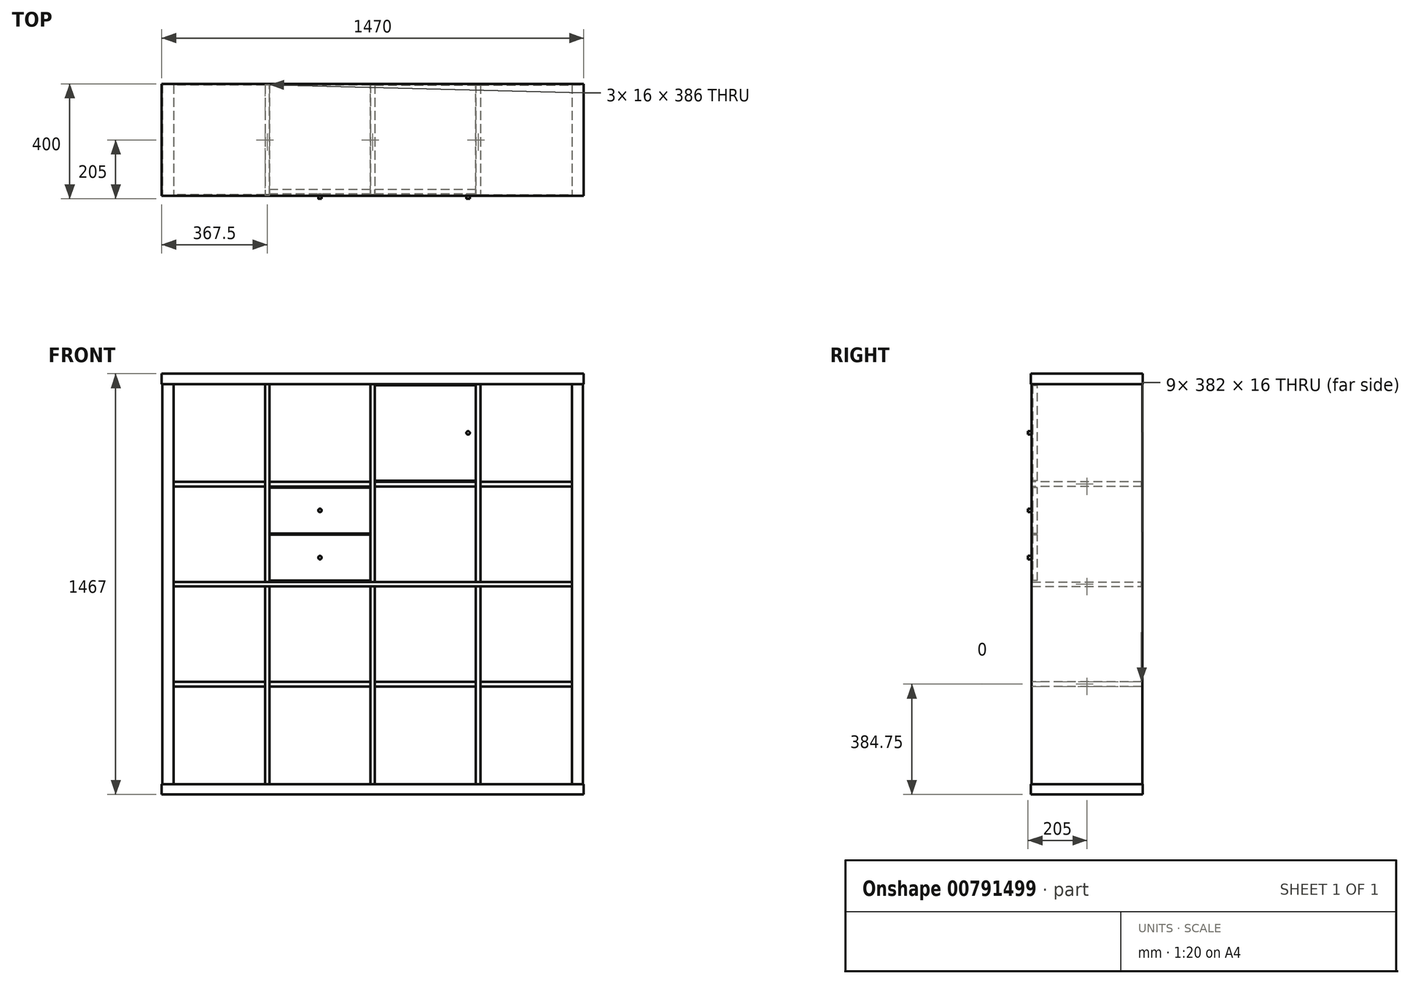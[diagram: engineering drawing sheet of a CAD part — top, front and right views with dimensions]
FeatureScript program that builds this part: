
annotation { "Feature Type Name" : "Feature", "Feature Type Description" : "" }
export const myFeature = defineFeature(function(context is Context, id is Id, definition is map)
    precondition{}
    {
        {
            var Q0;
            Q0=qCreatedBy(makeId("Top.planeOp"),FACE);
            var sketch = newSketch(context, id + "F0", { "sketchPlane" : qUnion([Q0])});
            skLineSegment(sketch, "E0.bottom", {"start": v(367.5, -97.5) * mm, "end": v(-367.5, -97.5) * mm});
            skLineSegment(sketch, "E0.top", {"start": v(367.5, 97.5) * mm, "end": v(-367.5, 97.5) * mm});
            skLineSegment(sketch, "E0.left", {"start": v(367.5, -97.5) * mm, "end": v(367.5, 97.5) * mm});
            skLineSegment(sketch, "E0.right", {"start": v(-367.5, -97.5) * mm, "end": v(-367.5, 97.5) * mm});
            skPoint(sketch, "E0.middle", {"position": v(0, 0) * mm});
            skLineSegment(sketch, "E1", {"start": v(-365.5, 97.5) * mm, "end": v(-365.5, -97.5) * mm});
            skLineSegment(sketch, "E2", {"start": v(-329.5, 97.5) * mm, "end": v(-329.5, -97.5) * mm});
            skSolve(sketch);
        }
        {
            var Q0;
            Q0 = qSketchRegion(id + "F0", true);
            var Q1;
            Q1=makeQuery(id+"F0.imprint","IMPRINT",FACE,{"disambiguationData":[TD([[makeQuery(id+"F0.imprint","IMPRINT",EDGE,{"derivedFrom":sQuery(id+"F0.wireOp",EDGE,"E0.bottom")}),-1.0]])]});
            extrude(context, id + "F1", {"entities" : qUnion([Q0, Q1]), "depth" : 36 * mm, "offsetDistance" : 25 * mm});
        }
        {
            var Q0;
            Q0=makeQuery(id+"F1.opExtrude","CAP_FACE",FACE,{"disambiguationData":[OSD([sQuery(id+"F0.wireOp",EDGE,"E0.bottom"),sQuery(id+"F0.wireOp",EDGE,"E0.top"),sQuery(id+"F0.wireOp",EDGE,"E0.left"),sQuery(id+"F0.wireOp",EDGE,"E0.right")])],"isStart":false});
            var sketch = newSketch(context, id + "F2", { "sketchPlane" : qUnion([Q0])});
            skLineSegment(sketch, "E3", {"start": v(-365.5, 97.5) * mm, "end": v(-365.5, -97.5) * mm});
            skLineSegment(sketch, "E4", {"start": v(-326.5, 97.5) * mm, "end": v(-326.5, -97.5) * mm});
            skLineSegment(sketch, "E5", {"start": v(-326.5, -95.5) * mm, "end": v(-365.5, -95.5) * mm});
            skSolve(sketch);
        }
        {
            var Q0;
            {var subQ3=sQuery(id+"F2.wireOp",EDGE,"E5");Q0=makeQuery(id+"F2.imprint","IMPRINT",FACE,{"disambiguationData":[TD([[makeQuery(id+"F2.imprint","IMPRINT",EDGE,{"derivedFrom":subQ3}),-1.0]])]});}
            extrude(context, id + "F3", {"entities" : qUnion([Q0]), "operationType" : NewBodyOperationType.ADD, "depth" : (1395 / 2) * mm, "offsetDistance" : 25 * mm});
        }
        {
            var Q0;
            Q0=makeQuery(id+"F3.opExtrude","SWEPT_FACE",FACE,{"disambiguationData":[OSD([sQuery(id+"F2.wireOp",EDGE,"E4")])]});
            var sketch = newSketch(context, id + "F4", { "sketchPlane" : qUnion([Q0])});
            skLineSegment(sketch, "E6.0", {"start": v(97.5, 733.5) * mm, "end": v(-95.5, 733.5) * mm});
            skLineSegment(sketch, "E7", {"start": v(97.5, 725.5) * mm, "end": v(-95.5, 725.5) * mm});
            skLineSegment(sketch, "E8", {"start": v(-93.5, 725.5) * mm, "end": v(-93.5, 733.5) * mm});
            skLineSegment(sketch, "E9", {"start": v(97.5, 384.75) * mm, "end": v(-95.5, 384.75) * mm, "construction": true});
            skLineSegment(sketch, "E10", {"start": v(97.5, 392.75) * mm, "end": v(-95.5, 392.75) * mm});
            skLineSegment(sketch, "E11", {"start": v(97.5, 376.75) * mm, "end": v(-95.5, 376.75) * mm});
            skLineSegment(sketch, "E12", {"start": v(-93.5, 392.75) * mm, "end": v(-93.5, 376.75) * mm});
            skSolve(sketch);
        }
        {
            var Q0;
            Q0 = qSketchRegion(id + "F4", true);
            var Q1;
            {var subQ3=sQuery(id+"F4.wireOp",EDGE,"E8");Q1=makeQuery(id+"F4.imprint","IMPRINT",FACE,{"disambiguationData":[TD([[makeQuery(id+"F4.imprint","IMPRINT",EDGE,{"derivedFrom":subQ3}),-1.0]])]});}
            var Q2;
            {var subQ3=sQuery(id+"F4.wireOp",EDGE,"E12");Q2=makeQuery(id+"F4.imprint","IMPRINT",FACE,{"disambiguationData":[TD([[makeQuery(id+"F4.imprint","IMPRINT",EDGE,{"derivedFrom":subQ3}),1.0]])]});}
            var Q3;
            Q3=makeQuery(id+"F1.opExtrude","SWEPT_FACE",FACE,{"disambiguationData":[OSD([sQuery(id+"F0.wireOp",EDGE,"E0.left")])]});
            extrude(context, id + "F5", {"entities" : qUnion([Q0, Q1, Q2]), "operationType" : NewBodyOperationType.ADD, "endBound" : BoundingType.UP_TO_SURFACE, "depth" : 25 * mm, "endBoundEntityFace" : qUnion([Q3]), "offsetDistance" : 25 * mm});
        }
        {
            var Q0;
            Q0=makeQuery(id+"F1.opExtrude","CAP_FACE",FACE,{"disambiguationData":[OSD([sQuery(id+"F0.wireOp",EDGE,"E0.bottom"),sQuery(id+"F0.wireOp",EDGE,"E0.top"),sQuery(id+"F0.wireOp",EDGE,"E0.left"),sQuery(id+"F0.wireOp",EDGE,"E0.right")])],"isStart":false});
            var sketch = newSketch(context, id + "F6", { "sketchPlane" : qUnion([Q0])});
            skLineSegment(sketch, "E13", {"start": v(-326.5, 1) * mm, "end": v(367.5, 1) * mm, "construction": true});
            skLineSegment(sketch, "E14", {"start": v(0, 0) * mm, "end": v(0, 97.5) * mm, "construction": true});
            skLineSegment(sketch, "E15", {"start": v(0, 0) * mm, "end": v(0, -97.5) * mm, "construction": true});
            skLineSegment(sketch, "E16", {"start": v(8, 97.5) * mm, "end": v(8, -97.5) * mm});
            skLineSegment(sketch, "E17", {"start": v(-8, 97.5) * mm, "end": v(-8, -97.5) * mm});
            skLineSegment(sketch, "E18", {"start": v(8, -95.5) * mm, "end": v(-8, -95.5) * mm});
            skLineSegment(sketch, "E19.0", {"start": v(367.5, -97.5) * mm, "end": v(367.5, 97.5) * mm});
            skLineSegment(sketch, "E20", {"start": v(359.5, 97.5) * mm, "end": v(359.5, -97.5) * mm});
            skLineSegment(sketch, "E21", {"start": v(367.5, -95.5) * mm, "end": v(359.5, -95.5) * mm});
            skSolve(sketch);
        }
        {
            var Q0;
            Q0 = qSketchRegion(id + "F6", true);
            var Q1;
            {var subQ5=sQuery(id+"F6.wireOp",EDGE,"E18");Q1=makeQuery(id+"F6.imprint","IMPRINT",FACE,{"disambiguationData":[TD([[makeQuery(id+"F6.imprint","IMPRINT",EDGE,{"derivedFrom":subQ5}),-1.0]])]});}
            var Q2;
            {var subQ5=sQuery(id+"F6.wireOp",EDGE,"E21");Q2=makeQuery(id+"F6.imprint","IMPRINT",FACE,{"disambiguationData":[TD([[makeQuery(id+"F6.imprint","IMPRINT",EDGE,{"derivedFrom":subQ5}),-1.0]])]});}
            var Q3;
            Q3=makeQuery(id+"F5.opExtrude","SWEPT_FACE",FACE,{"disambiguationData":[OSD([sQuery(id+"F4.wireOp",EDGE,"E7")])]});
            extrude(context, id + "F7", {"entities" : qUnion([Q0, Q1, Q2]), "operationType" : NewBodyOperationType.ADD, "endBound" : BoundingType.UP_TO_SURFACE, "depth" : 25 * mm, "endBoundEntityFace" : qUnion([Q3]), "offsetDistance" : 25 * mm});
        }
        {
            var Q0;
            Q0=makeQuery(id+"F1.opExtrude","SWEPT_BODY",BODY,{"disambiguationData":[OSD([sQuery(id+"F0.wireOp",EDGE,"E0.bottom"),sQuery(id+"F0.wireOp",EDGE,"E0.top"),sQuery(id+"F0.wireOp",EDGE,"E0.left"),sQuery(id+"F0.wireOp",EDGE,"E0.right")])]});
            var Q1;
            Q1=makeQuery(id+"F5.boolean.opBoolean","MERGE",FACE,{"derivedFrom":[makeQuery(id+"F3.opExtrude","CAP_FACE",FACE,{"disambiguationData":[OSD([sQuery(id+"F0.wireOp",EDGE,"E0.top"),sQuery(id+"F2.wireOp",EDGE,"E3"),sQuery(id+"F2.wireOp",EDGE,"E4"),sQuery(id+"F2.wireOp",EDGE,"E5")])],"isStart":false}),makeQuery(id+"F5.opExtrude","SWEPT_FACE",FACE,{"disambiguationData":[OSD([sQuery(id+"F4.wireOp",EDGE,"E6.0")])]})]});
            mirror(context, id + "F8", {"operationType" : NewBodyOperationType.ADD, "entities" : qUnion([Q0]), "mirrorPlane" : qUnion([Q1])});
        }
        {
            var Q0;
            Q0=makeQuery(id+"F1.opExtrude","SWEPT_BODY",BODY,{"disambiguationData":[OSD([sQuery(id+"F0.wireOp",EDGE,"E0.bottom"),sQuery(id+"F0.wireOp",EDGE,"E0.top"),sQuery(id+"F0.wireOp",EDGE,"E0.left"),sQuery(id+"F0.wireOp",EDGE,"E0.right")])]});
            var Q1;
            {var subQ0=sQuery(id+"F0.wireOp",EDGE,"E0.left");var subQ1=makeQuery(id+"F7.boolean.opBoolean","MERGE",FACE,{"derivedFrom":[makeQuery(id+"F1.opExtrude","SWEPT_FACE",FACE,{"disambiguationData":[OSD([subQ0])]}),makeQuery(id+"F5.opExtrude","CAP_FACE",FACE,{"disambiguationData":[OSD([subQ0]),OD(0.0)],"isStart":false}),makeQuery(id+"F5.opExtrude","CAP_FACE",FACE,{"disambiguationData":[OSD([subQ0]),OD(1.0)],"isStart":false}),makeQuery(id+"F7.opExtrude","SWEPT_FACE",FACE,{"disambiguationData":[OSD([sQuery(id+"F6.wireOp",EDGE,"E19.0")])]})]});Q1=makeQuery(id+"F8.boolean.opBoolean","MERGE",FACE,{"derivedFrom":[subQ1,makeQuery(id+"F8.opPattern","COPY",FACE,{"derivedFrom":subQ1,"instanceName":"1"})]});}
            mirror(context, id + "F9", {"operationType" : NewBodyOperationType.ADD, "entities" : qUnion([Q0]), "mirrorPlane" : qUnion([Q1])});
        }
        {
            var Q0;
            Q0=makeQuery(id+"F1.opExtrude","SWEPT_BODY",BODY,{"disambiguationData":[OSD([sQuery(id+"F0.wireOp",EDGE,"E0.bottom"),sQuery(id+"F0.wireOp",EDGE,"E0.top"),sQuery(id+"F0.wireOp",EDGE,"E0.left"),sQuery(id+"F0.wireOp",EDGE,"E0.right")])]});
            var Q1;
            {var subQ0=sQuery(id+"F2.wireOp",EDGE,"E4");var subQ1=sQuery(id+"F0.wireOp",EDGE,"E0.left");var subQ2=sQuery(id+"F0.wireOp",EDGE,"E0.top");var subQ3=makeQuery(id+"F1.opExtrude","SWEPT_FACE",FACE,{"disambiguationData":[OSD([subQ2])]});var subQ4=makeQuery(id+"F3.opExtrude","SWEPT_FACE",FACE,{"disambiguationData":[OSD([subQ2])]});var subQ5=makeQuery(id+"F3.boolean.opBoolean","SPLIT",EDGE,{"disambiguationData":[TD([makeQuery(id+"F1.opExtrude","SWEPT_FACE",FACE,{"disambiguationData":[OSD([subQ1])]})])],"derivedFrom":makeQuery(id+"F1.opExtrude","CAP_EDGE",EDGE,{"disambiguationData":[OSD([subQ2])],"isStart":false})});var subQ6=makeQuery(id+"F3.opExtrude","SWEPT_EDGE",EDGE,{"disambiguationData":[OSD([subQ2,subQ0])]});var subQ7=makeQuery(id+"F7.boolean.opBoolean","MERGE",FACE,{"derivedFrom":[makeQuery(id+"F5.boolean.opBoolean","MERGE",FACE,{"derivedFrom":[makeQuery(id+"F3.boolean.opBoolean","MERGE",FACE,{"derivedFrom":[subQ3,subQ4]}),makeQuery(id+"F5.opExtrude","SWEPT_FACE",FACE,{"disambiguationData":[OSD([subQ2,subQ0]),TDD([makeQuery(id+"F4.imprint","IMPRINT",EDGE,{"disambiguationData":[TD([[makeQuery(id+"F4.imprint","INTERSECT",VERTEX,{"derivedFrom":[subQ6,sQuery(id+"F4.wireOp",EDGE,"E6.0")]}),-1.0]])],"derivedFrom":subQ6})])]}),makeQuery(id+"F5.opExtrude","SWEPT_FACE",FACE,{"disambiguationData":[OSD([subQ2,subQ0]),TDD([makeQuery(id+"F4.imprint","IMPRINT",EDGE,{"disambiguationData":[TD([[makeQuery(id+"F4.imprint","INTERSECT",VERTEX,{"derivedFrom":[subQ6,sQuery(id+"F4.wireOp",EDGE,"E10")]}),-1.0]])],"derivedFrom":subQ6})])]})]}),makeQuery(id+"F7.opExtrude","SWEPT_FACE",FACE,{"disambiguationData":[OSD([subQ2]),TDD([makeQuery(id+"F6.imprint","IMPRINT",EDGE,{"disambiguationData":[TD([[makeQuery(id+"F6.imprint","INTERSECT",VERTEX,{"derivedFrom":[subQ5,sQuery(id+"F6.wireOp",EDGE,"E19.0")]}),-1.0]])],"derivedFrom":subQ5})])]}),makeQuery(id+"F7.opExtrude","SWEPT_FACE",FACE,{"disambiguationData":[OSD([subQ2]),TDD([makeQuery(id+"F6.imprint","IMPRINT",EDGE,{"disambiguationData":[TD([[makeQuery(id+"F6.imprint","INTERSECT",VERTEX,{"derivedFrom":[subQ5,sQuery(id+"F6.wireOp",EDGE,"E16")]}),-1.0]])],"derivedFrom":subQ5})])]})]});var subQ8=makeQuery(id+"F8.boolean.opBoolean","MERGE",FACE,{"derivedFrom":[subQ7,makeQuery(id+"F8.opPattern","COPY",FACE,{"derivedFrom":subQ7,"instanceName":"1"})]});Q1=makeQuery(id+"F9.boolean.opBoolean","MERGE",FACE,{"derivedFrom":[subQ8,makeQuery(id+"F9.opPattern","COPY",FACE,{"derivedFrom":subQ8,"instanceName":"1"})]});}
            mirror(context, id + "F10", {"operationType" : NewBodyOperationType.ADD, "entities" : qUnion([Q0]), "mirrorPlane" : qUnion([Q1])});
        }
        {
            var Q0;
            {var subQ0=makeQuery(id+"F9.opPattern","COPY",FACE,{"derivedFrom":makeQuery(id+"F8.opPattern","COPY",FACE,{"derivedFrom":makeQuery(id+"F7.opExtrude","SWEPT_FACE",FACE,{"disambiguationData":[OSD([sQuery(id+"F6.wireOp",EDGE,"E20")])]}),"instanceName":"1"}),"instanceName":"1"});Q0=makeQuery(id+"F10.boolean.opBoolean","MERGE",FACE,{"derivedFrom":[subQ0,makeQuery(id+"F10.opPattern","COPY",FACE,{"derivedFrom":subQ0,"instanceName":"1"})]});}
            var sketch = newSketch(context, id + "F11", { "sketchPlane" : qUnion([Q0])});
            skLineSegment(sketch, "E22.0", {"start": v(-95.5, 741.5) * mm, "end": v(-95.5, 1431) * mm});
            skLineSegment(sketch, "E22.1", {"start": v(290.5, 1431) * mm, "end": v(-95.5, 1431) * mm});
            skLineSegment(sketch, "E22.2", {"start": v(288.5, 1090.25) * mm, "end": v(-93.5, 1090.25) * mm});
            skLineSegment(sketch, "E23", {"start": v(-91.5, 1431) * mm, "end": v(-91.5, 1090.25) * mm});
            skLineSegment(sketch, "E24", {"start": v(-75.5, 1090.25) * mm, "end": v(-75.5, 1431) * mm});
            skLineSegment(sketch, "E25", {"start": v(-91.5, 1427) * mm, "end": v(-75.5, 1427) * mm});
            skLineSegment(sketch, "E26", {"start": v(-75.5, 1094.25) * mm, "end": v(-91.5, 1094.25) * mm});
            skSolve(sketch);
        }
        {
            var Q0;
            {var subQ0=sQuery(id+"F11.wireOp",EDGE,"E25");Q0=makeQuery(id+"F11.imprint","IMPRINT",FACE,{"disambiguationData":[TD([[makeQuery(id+"F11.imprint","IMPRINT",EDGE,{"derivedFrom":subQ0}),-1.0]])]});}
            extrude(context, id + "F12", {"entities" : qUnion([Q0]), "operationType" : NewBodyOperationType.ADD, "endBound" : BoundingType.UP_TO_NEXT, "depth" : 25 * mm, "offsetDistance" : 25 * mm});
        }
        {
            var Q0;
            Q0=makeQuery(id+"F12.opExtrude","SWEPT_FACE",FACE,{"disambiguationData":[OSD([sQuery(id+"F11.wireOp",EDGE,"E23")])]});
            var sketch = newSketch(context, id + "F13", { "sketchPlane" : qUnion([Q0])});
            skLineSegment(sketch, "E27.0", {"start": v(727, 1094.25) * mm, "end": v(727, 1427) * mm});
            skLineSegment(sketch, "E28", {"start": v(727, 1260.62) * mm, "end": v(616.07, 1260.62) * mm, "construction": true});
            skCircle(sketch, "E29", {"center": v(700, 1260.62) * mm, "radius": 6 * mm});
            skSolve(sketch);
        }
        {
            var Q0;
            Q0=makeQuery(id+"F13.imprint","IMPRINT",FACE,{"disambiguationData":[TD([[makeQuery(id+"F13.imprint","IMPRINT",EDGE,{"derivedFrom":sQuery(id+"F13.wireOp",EDGE,"E29")}),1.0]])]});
            extrude(context, id + "F14", {"entities" : qUnion([Q0]), "operationType" : NewBodyOperationType.ADD, "depth" : 16 * mm, "offsetDistance" : 25 * mm});
        }
        {
            var Q0;
            {var subQ0=makeQuery(id+"F8.opPattern","COPY",FACE,{"derivedFrom":makeQuery(id+"F7.opExtrude","SWEPT_FACE",FACE,{"disambiguationData":[OSD([sQuery(id+"F6.wireOp",EDGE,"E16")])]}),"instanceName":"1"});Q0=makeQuery(id+"F10.boolean.opBoolean","MERGE",FACE,{"derivedFrom":[subQ0,makeQuery(id+"F10.opPattern","COPY",FACE,{"derivedFrom":subQ0,"instanceName":"1"})]});}
            var sketch = newSketch(context, id + "F15", { "sketchPlane" : qUnion([Q0])});
            skLineSegment(sketch, "E30.0", {"start": v(288.5, 1074.25) * mm, "end": v(-93.5, 1074.25) * mm});
            skLineSegment(sketch, "E30.1", {"start": v(-95.5, 741.5) * mm, "end": v(-95.5, 1431) * mm});
            skLineSegment(sketch, "E30.2", {"start": v(-93.5, 741.5) * mm, "end": v(288.5, 741.5) * mm});
            skLineSegment(sketch, "E31", {"start": v(-91.5, 1074.25) * mm, "end": v(-91.5, 741.5) * mm});
            skLineSegment(sketch, "E32", {"start": v(-75.5, 741.5) * mm, "end": v(-75.5, 1074.25) * mm});
            skLineSegment(sketch, "E33", {"start": v(-75.5, 1070.25) * mm, "end": v(-91.5, 1070.25) * mm});
            skLineSegment(sketch, "E34", {"start": v(-75.5, 745.5) * mm, "end": v(-91.5, 745.5) * mm});
            skLineSegment(sketch, "E35", {"start": v(-75.5, 907.87) * mm, "end": v(-91.5, 907.87) * mm, "construction": true});
            skLineSegment(sketch, "E36", {"start": v(-75.5, 909.87) * mm, "end": v(-91.5, 909.87) * mm});
            skLineSegment(sketch, "E37", {"start": v(-91.5, 905.87) * mm, "end": v(-75.5, 905.87) * mm});
            skSolve(sketch);
        }
        {
            var Q0;
            {var subQ0=sQuery(id+"F15.wireOp",EDGE,"E33");Q0=makeQuery(id+"F15.imprint","IMPRINT",FACE,{"disambiguationData":[TD([[makeQuery(id+"F15.imprint","IMPRINT",EDGE,{"derivedFrom":subQ0}),1.0]])]});}
            var Q1;
            {var subQ0=sQuery(id+"F15.wireOp",EDGE,"E34");Q1=makeQuery(id+"F15.imprint","IMPRINT",FACE,{"disambiguationData":[TD([[makeQuery(id+"F15.imprint","IMPRINT",EDGE,{"derivedFrom":subQ0}),-1.0]])]});}
            extrude(context, id + "F16", {"entities" : qUnion([Q0, Q1]), "operationType" : NewBodyOperationType.ADD, "endBound" : BoundingType.UP_TO_NEXT, "depth" : 25 * mm, "offsetDistance" : 25 * mm});
        }
        {
            var Q0;
            {var subQ0=sQuery(id+"F15.wireOp",EDGE,"E31");Q0=makeQuery(id+"F16.opExtrude","SWEPT_FACE",FACE,{"disambiguationData":[OSD([subQ0]),TDD([makeQuery(id+"F15.imprint","IMPRINT",EDGE,{"disambiguationData":[TD([[makeQuery(id+"F15.imprint","INTERSECT",VERTEX,{"derivedFrom":[subQ0,sQuery(id+"F15.wireOp",EDGE,"E33")]}),-1.0]])],"derivedFrom":subQ0})])]});}
            var sketch = newSketch(context, id + "F17", { "sketchPlane" : qUnion([Q0])});
            skLineSegment(sketch, "E38.0", {"start": v(359.5, 1070.25) * mm, "end": v(8, 1070.25) * mm});
            skLineSegment(sketch, "E38.1", {"start": v(359.5, 905.87) * mm, "end": v(8, 905.87) * mm});
            skLineSegment(sketch, "E39", {"start": v(183.75, 1070.25) * mm, "end": v(183.75, 836.57) * mm, "construction": true});
            skCircle(sketch, "E40", {"center": v(183.75, 990.25) * mm, "radius": 6 * mm});
            skCircle(sketch, "E41", {"center": v(183.75, 825.87) * mm, "radius": 6 * mm});
            skSolve(sketch);
        }
        {
            var Q0;
            Q0 = qSketchRegion(id + "F17", true);
            extrude(context, id + "F18", {"entities" : qUnion([Q0]), "operationType" : NewBodyOperationType.ADD, "depth" : 16 * mm, "offsetDistance" : 25 * mm});
        }
    });
